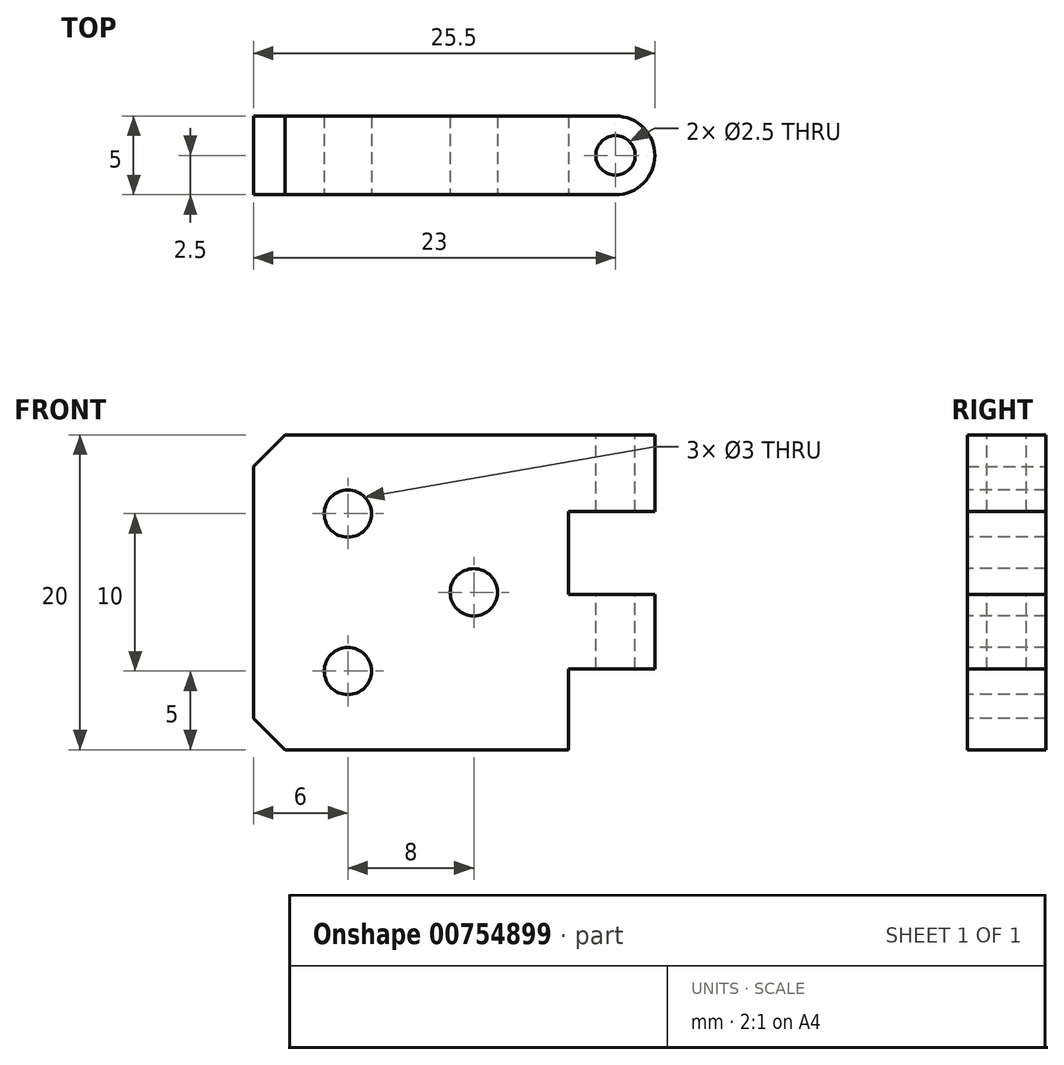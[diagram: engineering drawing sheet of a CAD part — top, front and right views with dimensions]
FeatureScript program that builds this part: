
annotation { "Feature Type Name" : "Feature", "Feature Type Description" : "" }
export const myFeature = defineFeature(function(context is Context, id is Id, definition is map)
    precondition{}
    {
        {
            var Q0;
            Q0=qCreatedBy(makeId("Front.planeOp"),FACE);
            var sketch = newSketch(context, id + "F0", { "sketchPlane" : qUnion([Q0])});
            skLineSegment(sketch, "E0.bottom", {"start": v(0, 0) * mm, "end": v(25.5, 0) * mm});
            skLineSegment(sketch, "E0.top", {"start": v(0, 20) * mm, "end": v(25.5, 20) * mm});
            skLineSegment(sketch, "E0.left", {"start": v(0, 0) * mm, "end": v(0, 20) * mm});
            skLineSegment(sketch, "E0.right", {"start": v(25.5, 0) * mm, "end": v(25.5, 20) * mm});
            skSolve(sketch);
        }
        {
            var Q0;
            Q0 = qSketchRegion(id + "F0", true);
            extrude(context, id + "F1", {"entities" : qUnion([Q0]), "depth" : 5 * mm, "offsetDistance" : 25 * mm});
        }
        {
            var Q0;
            Q0=makeQuery(id+"F1.opExtrude","CAP_EDGE",EDGE,{"disambiguationData":[OSD([sQuery(id+"F0.wireOp",EDGE,"E0.right")])],"isStart":false});
            var Q1;
            Q1=makeQuery(id+"F1.opExtrude","CAP_EDGE",EDGE,{"disambiguationData":[OSD([sQuery(id+"F0.wireOp",EDGE,"E0.right")])],"isStart":true});
            fillet(context, id + "F2", {"entities" : qUnion([Q0, Q1]), "radius" : 2.5 * mm, "tangentPropagation" : true, "allowEdgeOverflow" : false});
        }
        {
            var Q0;
            Q0=makeQuery(id+"F1.opExtrude","SWEPT_FACE",FACE,{"disambiguationData":[OSD([sQuery(id+"F0.wireOp",EDGE,"E0.top")])]});
            var sketch = newSketch(context, id + "F3", { "sketchPlane" : qUnion([Q0])});
            skCircle(sketch, "E1", {"center": v(23, -2.5) * mm, "radius": 1.25 * mm});
            skSolve(sketch);
        }
        {
            var Q0;
            Q0=makeQuery(id+"F3.imprint","IMPRINT",FACE,{"disambiguationData":[TD([[makeQuery(id+"F3.imprint","IMPRINT",EDGE,{"derivedFrom":sQuery(id+"F3.wireOp",EDGE,"E1")}),1.0]])]});
            extrude(context, id + "F4", {"entities" : qUnion([Q0]), "operationType" : NewBodyOperationType.REMOVE, "oppositeDirection" : true, "depth" : 25 * mm, "offsetDistance" : 25 * mm});
        }
        {
            var Q0;
            Q0=makeQuery(id+"F1.opExtrude","CAP_FACE",FACE,{"disambiguationData":[OSD([sQuery(id+"F0.wireOp",EDGE,"E0.bottom"),sQuery(id+"F0.wireOp",EDGE,"E0.top"),sQuery(id+"F0.wireOp",EDGE,"E0.left"),sQuery(id+"F0.wireOp",EDGE,"E0.right")])],"isStart":false});
            var sketch = newSketch(context, id + "F5", { "sketchPlane" : qUnion([Q0])});
            skLineSegment(sketch, "E2.bottom", {"start": v(20, 15.12) * mm, "end": v(29.49, 15.12) * mm});
            skLineSegment(sketch, "E2.top", {"start": v(20, 9.87) * mm, "end": v(29.49, 9.87) * mm});
            skLineSegment(sketch, "E2.left", {"start": v(20, 15.12) * mm, "end": v(20, 9.87) * mm});
            skLineSegment(sketch, "E2.right", {"start": v(29.49, 15.12) * mm, "end": v(29.49, 9.87) * mm});
            skLineSegment(sketch, "E3.bottom", {"start": v(20, 0) * mm, "end": v(29.34, 0) * mm});
            skLineSegment(sketch, "E3.top", {"start": v(20, 5.12) * mm, "end": v(29.34, 5.12) * mm});
            skLineSegment(sketch, "E3.left", {"start": v(20, 0) * mm, "end": v(20, 5.12) * mm});
            skLineSegment(sketch, "E3.right", {"start": v(29.34, 0) * mm, "end": v(29.34, 5.12) * mm});
            skSolve(sketch);
        }
        {
            var Q0;
            Q0 = qSketchRegion(id + "F5", true);
            extrude(context, id + "F6", {"entities" : qUnion([Q0]), "operationType" : NewBodyOperationType.REMOVE, "endBound" : BoundingType.THROUGH_ALL, "oppositeDirection" : true, "depth" : 25 * mm, "offsetDistance" : 25 * mm});
        }
        {
            var Q0;
            Q0=makeQuery(id+"F1.opExtrude","CAP_FACE",FACE,{"disambiguationData":[OSD([sQuery(id+"F0.wireOp",EDGE,"E0.bottom"),sQuery(id+"F0.wireOp",EDGE,"E0.top"),sQuery(id+"F0.wireOp",EDGE,"E0.left"),sQuery(id+"F0.wireOp",EDGE,"E0.right")])],"isStart":false});
            var sketch = newSketch(context, id + "F7", { "sketchPlane" : qUnion([Q0])});
            skCircle(sketch, "E4", {"center": v(6, 15) * mm, "radius": 1.5 * mm});
            skCircle(sketch, "E5", {"center": v(6, 5) * mm, "radius": 1.5 * mm});
            skCircle(sketch, "E6", {"center": v(14, 10) * mm, "radius": 1.5 * mm});
            skSolve(sketch);
        }
        {
            var Q0;
            Q0=makeQuery(id+"F7.imprint","IMPRINT",FACE,{"disambiguationData":[TD([[makeQuery(id+"F7.imprint","IMPRINT",EDGE,{"derivedFrom":sQuery(id+"F7.wireOp",EDGE,"E6")}),1.0]])]});
            var Q1;
            Q1=makeQuery(id+"F7.imprint","IMPRINT",FACE,{"disambiguationData":[TD([[makeQuery(id+"F7.imprint","IMPRINT",EDGE,{"derivedFrom":sQuery(id+"F7.wireOp",EDGE,"E4")}),1.0]])]});
            var Q2;
            Q2=makeQuery(id+"F7.imprint","IMPRINT",FACE,{"disambiguationData":[TD([[makeQuery(id+"F7.imprint","IMPRINT",EDGE,{"derivedFrom":sQuery(id+"F7.wireOp",EDGE,"E5")}),1.0]])]});
            extrude(context, id + "F8", {"entities" : qUnion([Q0, Q1, Q2]), "operationType" : NewBodyOperationType.REMOVE, "oppositeDirection" : true, "depth" : 25 * mm, "offsetDistance" : 25 * mm});
        }
        {
            var Q0;
            Q0=makeQuery(id+"F1.opExtrude","SWEPT_EDGE",EDGE,{"disambiguationData":[OSD([sQuery(id+"F0.wireOp",EDGE,"E0.top"),sQuery(id+"F0.wireOp",EDGE,"E0.left")])]});
            var Q1;
            Q1=makeQuery(id+"F1.opExtrude","SWEPT_EDGE",EDGE,{"disambiguationData":[OSD([sQuery(id+"F0.wireOp",EDGE,"E0.bottom"),sQuery(id+"F0.wireOp",EDGE,"E0.left")])]});
            chamfer(context, id + "F9", {"entities" : qUnion([Q0, Q1]), "width" : 2 * mm, "tangentPropagation" : true});
        }
    });
